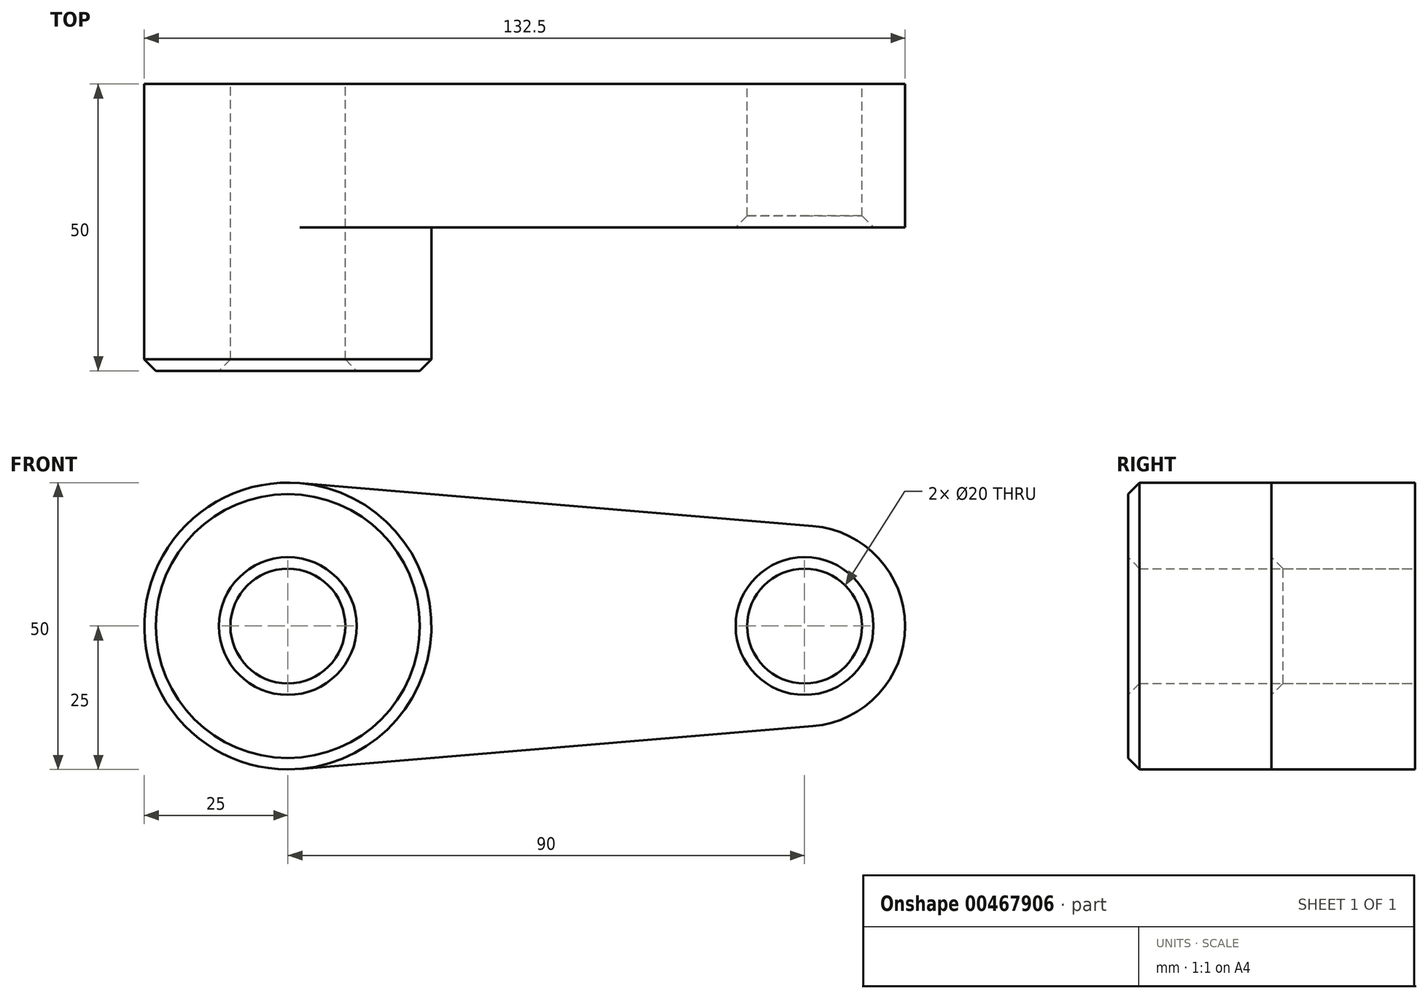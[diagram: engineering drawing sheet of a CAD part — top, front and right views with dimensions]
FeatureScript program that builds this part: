
annotation { "Feature Type Name" : "Feature", "Feature Type Description" : "" }
export const myFeature = defineFeature(function(context is Context, id is Id, definition is map)
    precondition{}
    {
        {
            var Q0;
            Q0=qCreatedBy(makeId("Front.planeOp"),FACE);
            var sketch = newSketch(context, id + "F0", { "sketchPlane" : qUnion([Q0])});
            skCircle(sketch, "E0", {"center": v(0, 0) * mm, "radius": 25 * mm});
            skCircle(sketch, "E1", {"center": v(90, 0) * mm, "radius": 17.5 * mm});
            skLineSegment(sketch, "E2", {"start": v(2.08, 24.91) * mm, "end": v(91.46, 17.44) * mm});
            skLineSegment(sketch, "E3", {"start": v(2.08, -24.91) * mm, "end": v(91.46, -17.44) * mm});
            skCircle(sketch, "E4", {"center": v(0, 0) * mm, "radius": 10 * mm});
            skCircle(sketch, "E5", {"center": v(90, 0) * mm, "radius": 10 * mm});
            skSolve(sketch);
        }
        {
            var Q0;
            Q0=qSketchRegion(id+"F0",true);
            extrude(context, id + "F1", {"entities" : qUnion([Q0]), "depth" : 25 * mm});
        }
        {
            var Q0;
            Q0=makeQuery(id+"F0.imprint","IMPRINT",FACE,{"disambiguationData":[TD([[makeQuery(id+"F0.imprint","IMPRINT",EDGE,{"derivedFrom":sQuery(id+"F0.wireOp",EDGE,"E4")}),-1.0]])]});
            extrude(context, id + "F2", {"entities" : qUnion([Q0]), "operationType" : NewBodyOperationType.ADD, "depth" : 50 * mm});
        }
        {
            var Q0;
            Q0=makeQuery(id+"F2.opExtrude","CAP_EDGE",EDGE,{"disambiguationData":[OSD([sQuery(id+"F0.wireOp",EDGE,"E0")])],"isStart":false});
            var Q1;
            Q1=makeQuery(id+"F2.opExtrude","CAP_EDGE",EDGE,{"disambiguationData":[OSD([sQuery(id+"F0.wireOp",EDGE,"E4")])],"isStart":false});
            var Q2;
            Q2=makeQuery(id+"F1.opExtrude","CAP_EDGE",EDGE,{"disambiguationData":[OSD([sQuery(id+"F0.wireOp",EDGE,"E5")])],"isStart":false});
            chamfer(context, id + "F3", {"entities" : qUnion([Q0, Q1, Q2]), "width" : 2 * mm, "tangentPropagation" : true});
        }
        {
            var Q0;
            Q0 = qSketchRegion(id + "F0", true);
            var sketch = newSketch(context, id + "F4", { "sketchPlane" : qUnion([Q0])});
            skSolve(sketch);
        }
        {
            var Q0;
            Q0=sQuery(id+"F0.wireOp",EDGE,"E4");
            extrude(context, id + "F5", {"bodyType" : ToolBodyType.SURFACE, "surfaceEntities" : qUnion([Q0]), "depth" : 25 * mm});
        }
    });
